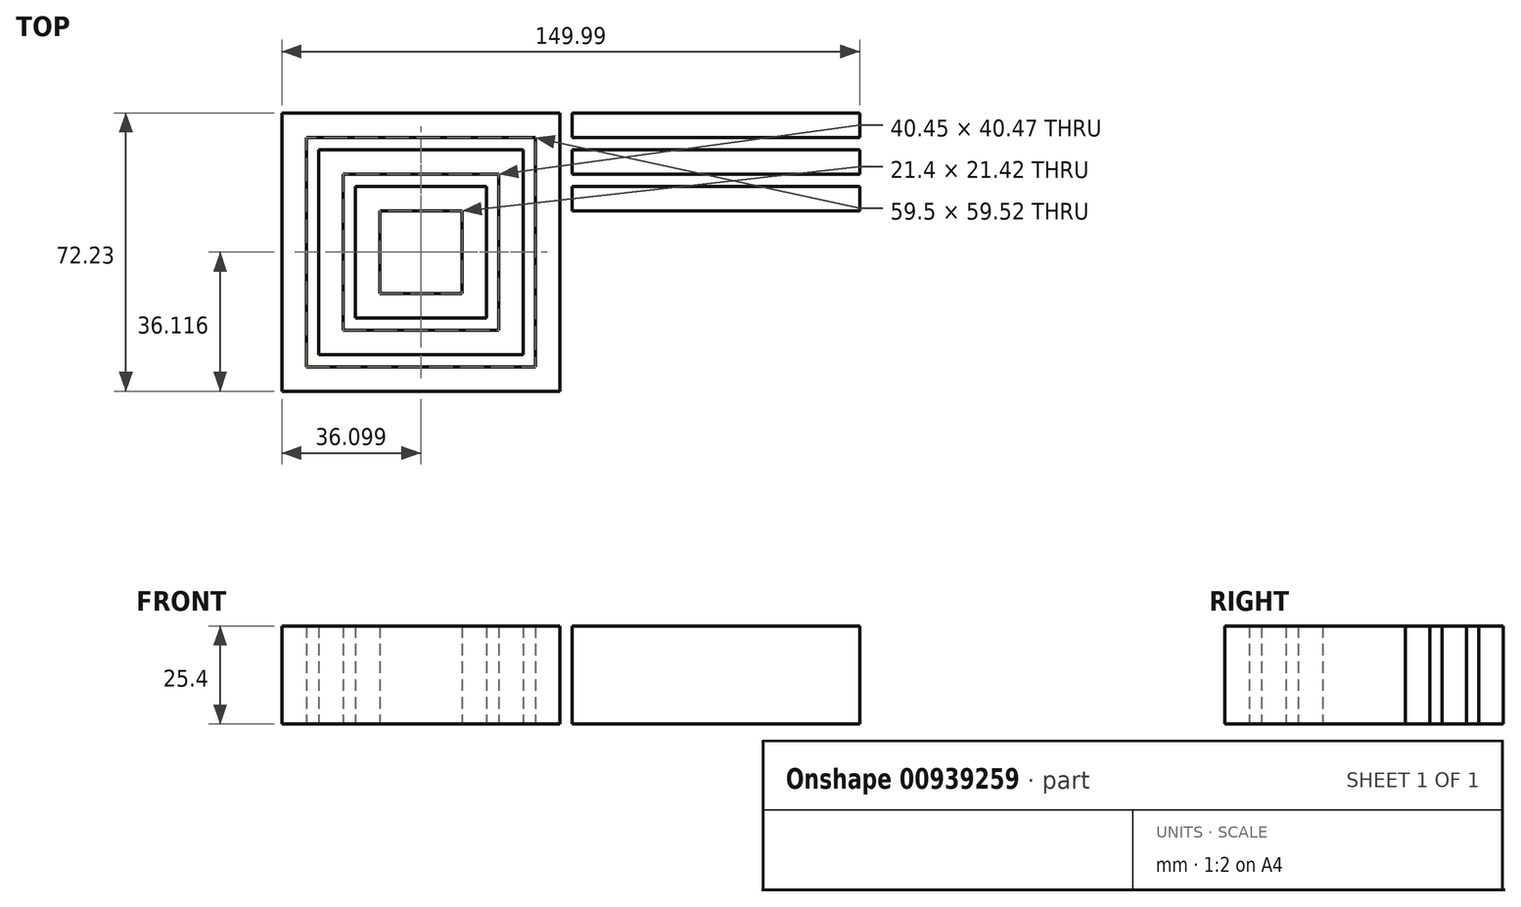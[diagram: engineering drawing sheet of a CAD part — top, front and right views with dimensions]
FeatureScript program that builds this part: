
annotation { "Feature Type Name" : "Feature", "Feature Type Description" : "" }
export const myFeature = defineFeature(function(context is Context, id is Id, definition is map)
    precondition{}
    {
        {
            var Q0;
            Q0=qCreatedBy(makeId("Top.planeOp"),FACE);
            var sketch = newSketch(context, id + "F0", { "sketchPlane" : qUnion([Q0])});
            skLineSegment(sketch, "E0.bottom", {"start": v(-65.58, 65.98) * mm, "end": v(-86.98, 65.98) * mm});
            skLineSegment(sketch, "E0.top", {"start": v(-65.58, 87.4) * mm, "end": v(-86.98, 87.4) * mm});
            skLineSegment(sketch, "E0.left", {"start": v(-65.58, 65.98) * mm, "end": v(-65.58, 87.4) * mm});
            skLineSegment(sketch, "E0.right", {"start": v(-86.98, 65.98) * mm, "end": v(-86.98, 87.4) * mm});
            skPoint(sketch, "E0.middle", {"position": v(-76.28, 76.7) * mm});
            skLineSegment(sketch, "E1.0", {"start": v(-59.23, 93.76) * mm, "end": v(-93.33, 93.76) * mm});
            skLineSegment(sketch, "E1.1", {"start": v(-59.23, 59.63) * mm, "end": v(-59.23, 93.76) * mm});
            skLineSegment(sketch, "E1.2", {"start": v(-59.23, 59.63) * mm, "end": v(-93.33, 59.63) * mm});
            skLineSegment(sketch, "E1.3", {"start": v(-93.33, 59.63) * mm, "end": v(-93.33, 93.76) * mm});
            skLineSegment(sketch, "E2.0", {"start": v(-56.05, 96.93) * mm, "end": v(-96.5, 96.93) * mm});
            skLineSegment(sketch, "E2.1", {"start": v(-56.05, 56.46) * mm, "end": v(-56.05, 96.93) * mm});
            skLineSegment(sketch, "E2.2", {"start": v(-56.05, 56.46) * mm, "end": v(-96.5, 56.46) * mm});
            skLineSegment(sketch, "E2.3", {"start": v(-96.5, 56.46) * mm, "end": v(-96.5, 96.93) * mm});
            skLineSegment(sketch, "E3.0", {"start": v(-49.7, 103.28) * mm, "end": v(-102.86, 103.28) * mm});
            skLineSegment(sketch, "E3.1", {"start": v(-49.7, 50.1) * mm, "end": v(-49.7, 103.28) * mm});
            skLineSegment(sketch, "E3.2", {"start": v(-49.7, 50.1) * mm, "end": v(-102.86, 50.1) * mm});
            skLineSegment(sketch, "E3.3", {"start": v(-102.86, 50.1) * mm, "end": v(-102.86, 103.28) * mm});
            skLineSegment(sketch, "E4.0", {"start": v(-46.53, 106.46) * mm, "end": v(-106.03, 106.46) * mm});
            skLineSegment(sketch, "E4.1", {"start": v(-46.53, 46.93) * mm, "end": v(-46.53, 106.46) * mm});
            skLineSegment(sketch, "E4.2", {"start": v(-46.53, 46.93) * mm, "end": v(-106.03, 46.93) * mm});
            skLineSegment(sketch, "E4.3", {"start": v(-106.03, 46.93) * mm, "end": v(-106.03, 106.46) * mm});
            skLineSegment(sketch, "E5.0", {"start": v(-40.18, 112.8) * mm, "end": v(-112.38, 112.8) * mm});
            skLineSegment(sketch, "E5.1", {"start": v(-40.18, 40.58) * mm, "end": v(-40.18, 112.8) * mm});
            skLineSegment(sketch, "E5.2", {"start": v(-40.18, 40.58) * mm, "end": v(-112.38, 40.58) * mm});
            skLineSegment(sketch, "E5.3", {"start": v(-112.38, 40.58) * mm, "end": v(-112.38, 112.8) * mm});
            skLineSegment(sketch, "E6", {"start": v(-65.58, 87.4) * mm, "end": v(-59.23, 93.76) * mm});
            skLineSegment(sketch, "E7", {"start": v(-56.05, 96.93) * mm, "end": v(-49.7, 103.28) * mm});
            skLineSegment(sketch, "E8", {"start": v(-46.53, 106.46) * mm, "end": v(-40.18, 112.8) * mm});
            skLineSegment(sketch, "E9", {"start": v(-65.58, 65.98) * mm, "end": v(-59.23, 59.63) * mm});
            skLineSegment(sketch, "E10", {"start": v(-56.05, 56.46) * mm, "end": v(-49.7, 50.1) * mm});
            skLineSegment(sketch, "E11", {"start": v(-46.53, 46.93) * mm, "end": v(-40.18, 40.58) * mm});
            skLineSegment(sketch, "E12", {"start": v(-86.98, 87.4) * mm, "end": v(-93.33, 93.76) * mm});
            skLineSegment(sketch, "E13", {"start": v(-96.5, 96.93) * mm, "end": v(-102.86, 103.28) * mm});
            skLineSegment(sketch, "E14", {"start": v(-106.03, 106.46) * mm, "end": v(-112.38, 112.8) * mm});
            skLineSegment(sketch, "E15", {"start": v(-86.98, 65.98) * mm, "end": v(-93.33, 59.63) * mm});
            skLineSegment(sketch, "E16", {"start": v(-96.5, 56.46) * mm, "end": v(-102.86, 50.1) * mm});
            skLineSegment(sketch, "E17", {"start": v(-106.03, 46.93) * mm, "end": v(-112.38, 40.58) * mm});
            skLineSegment(sketch, "E18.0", {"start": v(-37, 40.58) * mm, "end": v(-37, 93.76) * mm});
            skLineSegment(sketch, "E19", {"start": v(-37, 112.8) * mm, "end": v(37.61, 112.8) * mm});
            skLineSegment(sketch, "E20.0", {"start": v(-37, 106.46) * mm, "end": v(37.61, 106.46) * mm});
            skLineSegment(sketch, "E21.0", {"start": v(-37, 103.28) * mm, "end": v(37.61, 103.28) * mm});
            skLineSegment(sketch, "E22.0", {"start": v(-37, 96.93) * mm, "end": v(37.61, 96.93) * mm});
            skLineSegment(sketch, "E23.0", {"start": v(-37, 93.76) * mm, "end": v(37.61, 93.76) * mm});
            skLineSegment(sketch, "E24.0", {"start": v(-37, 87.4) * mm, "end": v(37.61, 87.4) * mm});
            skLineSegment(sketch, "E25.trimOffspring", {"start": v(-37, 106.46) * mm, "end": v(-37, 112.8) * mm});
            skLineSegment(sketch, "E26.trimOffspring", {"start": v(-37, 96.93) * mm, "end": v(-37, 103.28) * mm});
            skLineSegment(sketch, "E27", {"start": v(37.61, 112.8) * mm, "end": v(37.61, 106.46) * mm});
            skLineSegment(sketch, "E28", {"start": v(37.61, 103.28) * mm, "end": v(37.61, 96.93) * mm});
            skLineSegment(sketch, "E29", {"start": v(37.61, 93.76) * mm, "end": v(37.61, 87.4) * mm});
            skSolve(sketch);
        }
        {
            var Q0;
            Q0=makeQuery(id+"F0.imprint","IMPRINT",FACE,{"disambiguationData":[TD([[makeQuery(id+"F0.imprint","IMPRINT",EDGE,{"derivedFrom":sQuery(id+"F0.wireOp",EDGE,"E0.top")}),-1.0]])]});
            var Q1;
            Q1=makeQuery(id+"F0.imprint","IMPRINT",FACE,{"disambiguationData":[TD([[makeQuery(id+"F0.imprint","IMPRINT",EDGE,{"derivedFrom":sQuery(id+"F0.wireOp",EDGE,"E0.left")}),-1.0]])]});
            var Q2;
            Q2=makeQuery(id+"F0.imprint","IMPRINT",FACE,{"disambiguationData":[TD([[makeQuery(id+"F0.imprint","IMPRINT",EDGE,{"derivedFrom":sQuery(id+"F0.wireOp",EDGE,"E0.right")}),1.0]])]});
            var Q3;
            Q3=makeQuery(id+"F0.imprint","IMPRINT",FACE,{"disambiguationData":[TD([[makeQuery(id+"F0.imprint","IMPRINT",EDGE,{"derivedFrom":sQuery(id+"F0.wireOp",EDGE,"E0.bottom")}),1.0]])]});
            var Q4;
            Q4=makeQuery(id+"F0.imprint","IMPRINT",FACE,{"disambiguationData":[TD([[makeQuery(id+"F0.imprint","IMPRINT",EDGE,{"derivedFrom":sQuery(id+"F0.wireOp",EDGE,"E2.1")}),-1.0]])]});
            var Q5;
            Q5=makeQuery(id+"F0.imprint","IMPRINT",FACE,{"disambiguationData":[TD([[makeQuery(id+"F0.imprint","IMPRINT",EDGE,{"derivedFrom":sQuery(id+"F0.wireOp",EDGE,"E2.3")}),1.0]])]});
            var Q6;
            Q6=makeQuery(id+"F0.imprint","IMPRINT",FACE,{"disambiguationData":[TD([[makeQuery(id+"F0.imprint","IMPRINT",EDGE,{"derivedFrom":sQuery(id+"F0.wireOp",EDGE,"E2.2")}),1.0]])]});
            var Q7;
            Q7=makeQuery(id+"F0.imprint","IMPRINT",FACE,{"disambiguationData":[TD([[makeQuery(id+"F0.imprint","IMPRINT",EDGE,{"derivedFrom":sQuery(id+"F0.wireOp",EDGE,"E2.0")}),-1.0]])]});
            var Q8;
            Q8=makeQuery(id+"F0.imprint","IMPRINT",FACE,{"disambiguationData":[TD([[makeQuery(id+"F0.imprint","IMPRINT",EDGE,{"derivedFrom":sQuery(id+"F0.wireOp",EDGE,"E4.0")}),-1.0]])]});
            var Q9;
            Q9=makeQuery(id+"F0.imprint","IMPRINT",FACE,{"disambiguationData":[TD([[makeQuery(id+"F0.imprint","IMPRINT",EDGE,{"derivedFrom":sQuery(id+"F0.wireOp",EDGE,"E4.1")}),-1.0]])]});
            var Q10;
            Q10=makeQuery(id+"F0.imprint","IMPRINT",FACE,{"disambiguationData":[TD([[makeQuery(id+"F0.imprint","IMPRINT",EDGE,{"derivedFrom":sQuery(id+"F0.wireOp",EDGE,"E4.3")}),1.0]])]});
            var Q11;
            Q11=makeQuery(id+"F0.imprint","IMPRINT",FACE,{"disambiguationData":[TD([[makeQuery(id+"F0.imprint","IMPRINT",EDGE,{"derivedFrom":sQuery(id+"F0.wireOp",EDGE,"E4.2")}),1.0]])]});
            var Q12;
            Q12=makeQuery(id+"F0.imprint","IMPRINT",FACE,{"disambiguationData":[TD([[makeQuery(id+"F0.imprint","IMPRINT",EDGE,{"derivedFrom":sQuery(id+"F0.wireOp",EDGE,"E21.0")}),-1.0]])]});
            var Q13;
            Q13=makeQuery(id+"F0.imprint","IMPRINT",FACE,{"disambiguationData":[TD([[makeQuery(id+"F0.imprint","IMPRINT",EDGE,{"derivedFrom":sQuery(id+"F0.wireOp",EDGE,"E19")}),-1.0]])]});
            var Q14;
            {var subQ0=sQuery(id+"F0.wireOp",EDGE,"E23.0");Q14=makeQuery(id+"F0.imprint","IMPRINT",FACE,{"disambiguationData":[TD([[makeQuery(id+"F0.imprint","IMPRINT",EDGE,{"derivedFrom":subQ0}),-1.0]])]});}
            extrude(context, id + "F1", {"entities" : qUnion([Q0, Q1, Q2, Q3, Q4, Q5, Q6, Q7, Q8, Q9, Q10, Q11, Q12, Q13, Q14]), "depth" : 25.4 * mm, "offsetDistance" : 25.4 * mm});
        }
    });
